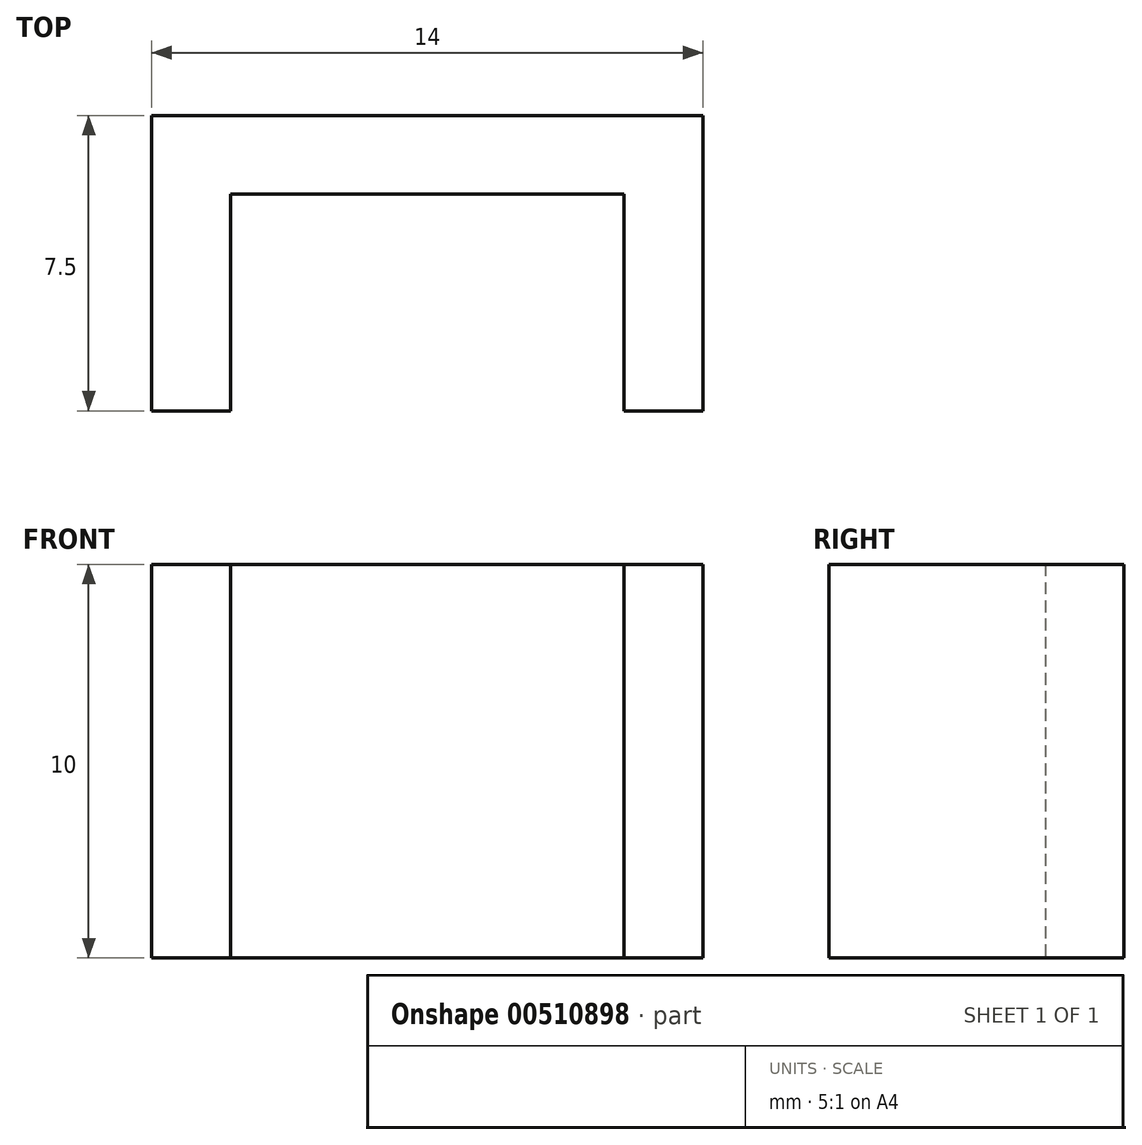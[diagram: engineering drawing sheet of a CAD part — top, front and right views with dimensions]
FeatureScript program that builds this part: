
annotation { "Feature Type Name" : "Feature", "Feature Type Description" : "" }
export const myFeature = defineFeature(function(context is Context, id is Id, definition is map)
    precondition{}
    {
        {
            var Q0;
            Q0=qCreatedBy(makeId("Top.planeOp"),FACE);
            var sketch = newSketch(context, id + "F0", { "sketchPlane" : qUnion([Q0])});
            skLineSegment(sketch, "E0.bottom", {"start": v(-5, 2.75) * mm, "end": v(5, 2.75) * mm});
            skLineSegment(sketch, "E0.left", {"start": v(-5, 2.75) * mm, "end": v(-5, -2.75) * mm});
            skLineSegment(sketch, "E0.right", {"start": v(5, 2.75) * mm, "end": v(5, -2.75) * mm});
            skLineSegment(sketch, "E1.bottom", {"start": v(-7, 4.75) * mm, "end": v(7, 4.75) * mm});
            skLineSegment(sketch, "E1.left", {"start": v(-7, 4.75) * mm, "end": v(-7, -2.75) * mm});
            skLineSegment(sketch, "E1.right", {"start": v(7, 4.75) * mm, "end": v(7, -2.75) * mm});
            skLineSegment(sketch, "E2", {"start": v(-7, -2.75) * mm, "end": v(-5, -2.75) * mm});
            skLineSegment(sketch, "E3", {"start": v(5, -2.75) * mm, "end": v(7, -2.75) * mm});
            skSolve(sketch);
        }
        {
            var Q0;
            Q0=makeQuery(id+"F0.imprint","IMPRINT",FACE,{"disambiguationData":[TD([[makeQuery(id+"F0.imprint","IMPRINT",EDGE,{"derivedFrom":sQuery(id+"F0.wireOp",EDGE,"E0.bottom")}),1.0]])]});
            extrude(context, id + "F1", {"entities" : qUnion([Q0]), "depth" : 10 * mm});
        }
    });
